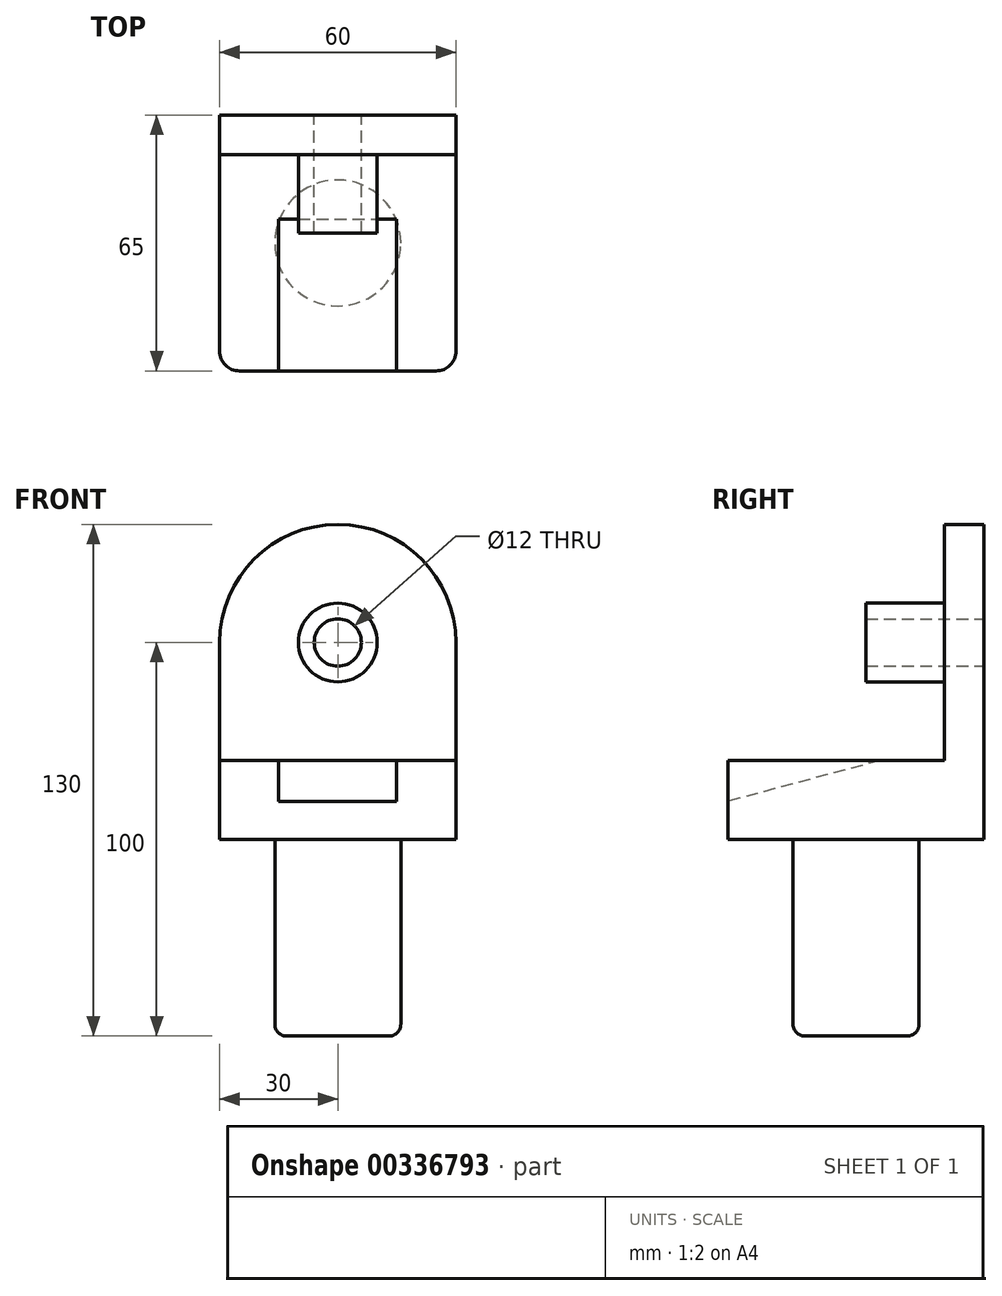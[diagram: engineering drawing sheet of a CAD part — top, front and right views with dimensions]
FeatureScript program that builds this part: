
annotation { "Feature Type Name" : "Feature", "Feature Type Description" : "" }
export const myFeature = defineFeature(function(context is Context, id is Id, definition is map)
    precondition{}
    {
        {
            var Q0;
            Q0=qCreatedBy(makeId("Top.planeOp"),FACE);
            var sketch = newSketch(context, id + "F0", { "sketchPlane" : qUnion([Q0])});
            skCircle(sketch, "E0", {"center": v(0, 0) * mm, "radius": 16 * mm});
            skSolve(sketch);
        }
        {
            var Q0;
            Q0 = qSketchRegion(id + "F0", true);
            extrude(context, id + "F1", {"entities" : qUnion([Q0]), "depth" : 50 * mm});
        }
        {
            var Q0;
            Q0=makeQuery(id+"F1.opExtrude","CAP_FACE",FACE,{"disambiguationData":[OSD([sQuery(id+"F0.wireOp",EDGE,"E0")])],"isStart":false});
            var sketch = newSketch(context, id + "F2", { "sketchPlane" : qUnion([Q0])});
            skLineSegment(sketch, "E1", {"start": v(-30, 0) * mm, "end": v(-30, -32.5) * mm});
            skLineSegment(sketch, "E2", {"start": v(-30, 0) * mm, "end": v(-30, 32.5) * mm});
            skLineSegment(sketch, "E3", {"start": v(-30, -32.5) * mm, "end": v(30, -32.5) * mm});
            skLineSegment(sketch, "E4", {"start": v(30, -32.5) * mm, "end": v(30, 0) * mm});
            skLineSegment(sketch, "E5", {"start": v(30, 0) * mm, "end": v(30, 32.5) * mm});
            skLineSegment(sketch, "E6", {"start": v(30, 32.5) * mm, "end": v(-30, 32.5) * mm});
            skLineSegment(sketch, "E7", {"start": v(-30, 32.5) * mm, "end": v(-30, 22.5) * mm});
            skLineSegment(sketch, "E8", {"start": v(-30, 22.5) * mm, "end": v(30, 22.5) * mm});
            skPoint(sketch, "E9.start.orphan", {"position": v(0, 0) * mm});
            skSolve(sketch);
        }
        {
            var Q0;
            Q0=makeQuery(id+"F2.imprint","IMPRINT",FACE,{"disambiguationData":[TD([[makeQuery(id+"F2.imprint","IMPRINT",EDGE,{"derivedFrom":makeQuery(id+"F1.opExtrude","CAP_EDGE",EDGE,{"disambiguationData":[OSD([sQuery(id+"F0.wireOp",EDGE,"E0")])],"isStart":false})}),1.0]])]});
            var Q1;
            Q1=makeQuery(id+"F2.imprint","IMPRINT",FACE,{"disambiguationData":[TD([[makeQuery(id+"F2.imprint","IMPRINT",EDGE,{"derivedFrom":sQuery(id+"F2.wireOp",EDGE,"E1")}),1.0]])]});
            extrude(context, id + "F3", {"entities" : qUnion([Q0, Q1]), "operationType" : NewBodyOperationType.ADD, "depth" : 20 * mm});
        }
        {
            var Q0;
            {var subQ0=sQuery(id+"F2.wireOp",EDGE,"E6");Q0=makeQuery(id+"F2.imprint","IMPRINT",FACE,{"disambiguationData":[TD([[makeQuery(id+"F2.imprint","IMPRINT",EDGE,{"derivedFrom":subQ0}),1.0]])]});}
            extrude(context, id + "F4", {"entities" : qUnion([Q0]), "operationType" : NewBodyOperationType.ADD, "depth" : 50 * mm});
        }
        {
            var Q0;
            Q0=makeQuery(id+"F4.opExtrude","SWEPT_FACE",FACE,{"disambiguationData":[OSD([sQuery(id+"F2.wireOp",EDGE,"E8")])]});
            var sketch = newSketch(context, id + "F5", { "sketchPlane" : qUnion([Q0])});
            skArc(sketch, "E10", {"start": v(30, 100) * mm, "mid": v(0, 130) * mm, "end": v(-30, 100) * mm});
            skCircle(sketch, "E11", {"center": v(0, 100) * mm, "radius": 6 * mm});
            skCircle(sketch, "E12", {"center": v(0, 100) * mm, "radius": 10 * mm});
            skLineSegment(sketch, "E13", {"start": v(-30, 100) * mm, "end": v(-10, 100) * mm});
            skLineSegment(sketch, "E14", {"start": v(10, 100) * mm, "end": v(30, 100) * mm});
            skSolve(sketch);
        }
        {
            var Q0;
            {var subQ0=sQuery(id+"F5.wireOp",EDGE,"E11");var subQ1=makeQuery(id+"F4.opExtrude","CAP_EDGE",EDGE,{"disambiguationData":[OSD([sQuery(id+"F2.wireOp",EDGE,"E8")])],"isStart":false});var subQ2=makeQuery(id+"F5.imprint","INTERSECT",VERTEX,{"disambiguationData":[OD(0.0)],"derivedFrom":[subQ1,subQ0]});Q0=makeQuery(id+"F5.imprint","IMPRINT",FACE,{"disambiguationData":[TD([[makeQuery(id+"F5.imprint","IMPRINT",EDGE,{"disambiguationData":[TD([[subQ2,-1.0]])],"derivedFrom":subQ0}),1.0]])]});}
            var Q1;
            {var subQ0=sQuery(id+"F5.wireOp",EDGE,"E11");var subQ1=makeQuery(id+"F4.opExtrude","CAP_EDGE",EDGE,{"disambiguationData":[OSD([sQuery(id+"F2.wireOp",EDGE,"E8")])],"isStart":false});var subQ2=makeQuery(id+"F5.imprint","INTERSECT",VERTEX,{"disambiguationData":[OD(0.0)],"derivedFrom":[subQ1,subQ0]});Q1=makeQuery(id+"F5.imprint","IMPRINT",FACE,{"disambiguationData":[TD([[makeQuery(id+"F5.imprint","IMPRINT",EDGE,{"disambiguationData":[TD([[subQ2,1.0]])],"derivedFrom":subQ0}),1.0]])]});}
            extrude(context, id + "F6", {"entities" : qUnion([Q0, Q1]), "operationType" : NewBodyOperationType.REMOVE, "depth" : 20 * mm, "hasSecondDirection" : true, "secondDirectionOppositeDirection" : true, "secondDirectionDepth" : 10 * mm});
        }
        {
            var Q0;
            {var subQ0=sQuery(id+"F5.wireOp",EDGE,"E11");var subQ1=makeQuery(id+"F4.opExtrude","CAP_EDGE",EDGE,{"disambiguationData":[OSD([sQuery(id+"F2.wireOp",EDGE,"E8")])],"isStart":false});var subQ2=makeQuery(id+"F5.imprint","INTERSECT",VERTEX,{"disambiguationData":[OD(0.0)],"derivedFrom":[subQ1,subQ0]});Q0=makeQuery(id+"F5.imprint","IMPRINT",FACE,{"disambiguationData":[TD([[makeQuery(id+"F5.imprint","IMPRINT",EDGE,{"disambiguationData":[TD([[subQ2,-1.0]])],"derivedFrom":subQ0}),-1.0]])]});}
            var Q1;
            {var subQ0=sQuery(id+"F5.wireOp",EDGE,"E11");var subQ1=makeQuery(id+"F4.opExtrude","CAP_EDGE",EDGE,{"disambiguationData":[OSD([sQuery(id+"F2.wireOp",EDGE,"E8")])],"isStart":false});var subQ2=makeQuery(id+"F5.imprint","INTERSECT",VERTEX,{"disambiguationData":[OD(0.0)],"derivedFrom":[subQ1,subQ0]});Q1=makeQuery(id+"F5.imprint","IMPRINT",FACE,{"disambiguationData":[TD([[makeQuery(id+"F5.imprint","IMPRINT",EDGE,{"disambiguationData":[TD([[subQ2,1.0]])],"derivedFrom":subQ0}),-1.0]])]});}
            extrude(context, id + "F7", {"entities" : qUnion([Q0, Q1]), "operationType" : NewBodyOperationType.ADD, "depth" : 20 * mm, "hasSecondDirection" : true, "secondDirectionOppositeDirection" : true, "secondDirectionDepth" : 10 * mm});
        }
        {
            var Q0;
            Q0=makeQuery(id+"F5.imprint","IMPRINT",FACE,{"disambiguationData":[TD([[makeQuery(id+"F5.imprint","IMPRINT",EDGE,{"derivedFrom":sQuery(id+"F5.wireOp",EDGE,"E10")}),1.0]])]});
            extrude(context, id + "F8", {"entities" : qUnion([Q0]), "operationType" : NewBodyOperationType.ADD, "oppositeDirection" : true, "depth" : 10 * mm});
        }
        {
            var Q0;
            Q0=makeQuery(id+"F3.opExtrude","SWEPT_EDGE",EDGE,{"disambiguationData":[OSD([sQuery(id+"F2.wireOp",EDGE,"E3"),sQuery(id+"F2.wireOp",EDGE,"E4")])]});
            fillet(context, id + "F9", {"entities" : qUnion([Q0]), "radius" : 5 * mm, "tangentPropagation" : true, "allowEdgeOverflow" : false});
        }
        {
            var Q0;
            Q0=makeQuery(id+"F3.opExtrude","SWEPT_EDGE",EDGE,{"disambiguationData":[OSD([sQuery(id+"F2.wireOp",EDGE,"E1"),sQuery(id+"F2.wireOp",EDGE,"E3")])]});
            fillet(context, id + "F10", {"entities" : qUnion([Q0]), "radius" : 5 * mm, "tangentPropagation" : true, "allowEdgeOverflow" : false});
        }
        {
            var Q0;
            Q0=qCreatedBy(makeId("Right.planeOp"),FACE);
            var sketch = newSketch(context, id + "F11", { "sketchPlane" : qUnion([Q0])});
            skLineSegment(sketch, "E15", {"start": v(-32.61, 70.08) * mm, "end": v(6.4, 70.08) * mm});
            skLineSegment(sketch, "E16", {"start": v(6.4, 70.08) * mm, "end": v(-32.61, 59.63) * mm});
            skLineSegment(sketch, "E17", {"start": v(-32.61, 70.08) * mm, "end": v(-32.61, 59.63) * mm});
            skSolve(sketch);
        }
        {
            var Q0;
            Q0 = qSketchRegion(id + "F11", true);
            extrude(context, id + "F12", {"entities" : qUnion([Q0]), "operationType" : NewBodyOperationType.REMOVE, "oppositeDirection" : true, "depth" : 15 * mm, "hasSecondDirection" : true, "secondDirectionOppositeDirection" : false, "secondDirectionDepth" : 14.9 * mm});
        }
        {
            var Q0;
            Q0=makeQuery(id+"F1.opExtrude","CAP_EDGE",EDGE,{"disambiguationData":[OSD([sQuery(id+"F0.wireOp",EDGE,"E0")])],"isStart":true});
            fillet(context, id + "F13", {"entities" : qUnion([Q0]), "radius" : 3 * mm, "tangentPropagation" : true, "allowEdgeOverflow" : false});
        }
    });
